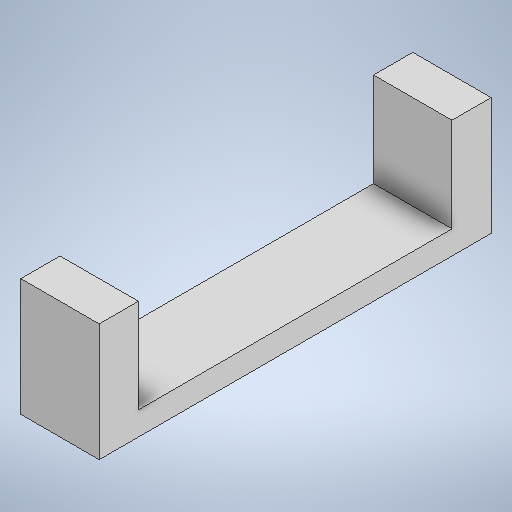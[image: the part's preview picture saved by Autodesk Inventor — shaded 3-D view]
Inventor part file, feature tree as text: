
AUTODESK INVENTOR PART (.ipt)
format: ipt  version: 2025.2 (Build 292293000, 293)  size: 222,208 bytes
history: native  units: mm
features: extrude x2, sketch x2
ambient origin geometry x8: Origin, YZ Plane, XZ Plane, XY Plane, X Axis, Y Axis, Z Axis, Center Point
bodies: Solid1 (feature_tree)
feature tree (4):
  extrude  "Extrusion1"  Depth=50.0mm
  extrude  "Extrusion2"  Depth=5.0mm
  sketch  "Sketch1"  dims[d0=10.0mm d1=50.0mm]
  sketch  "Sketch2"  dims[d2=3.0mm d3=0.0mm d4=5.0mm d5=5.0mm d6=12.0mm d7=0.0mm]
